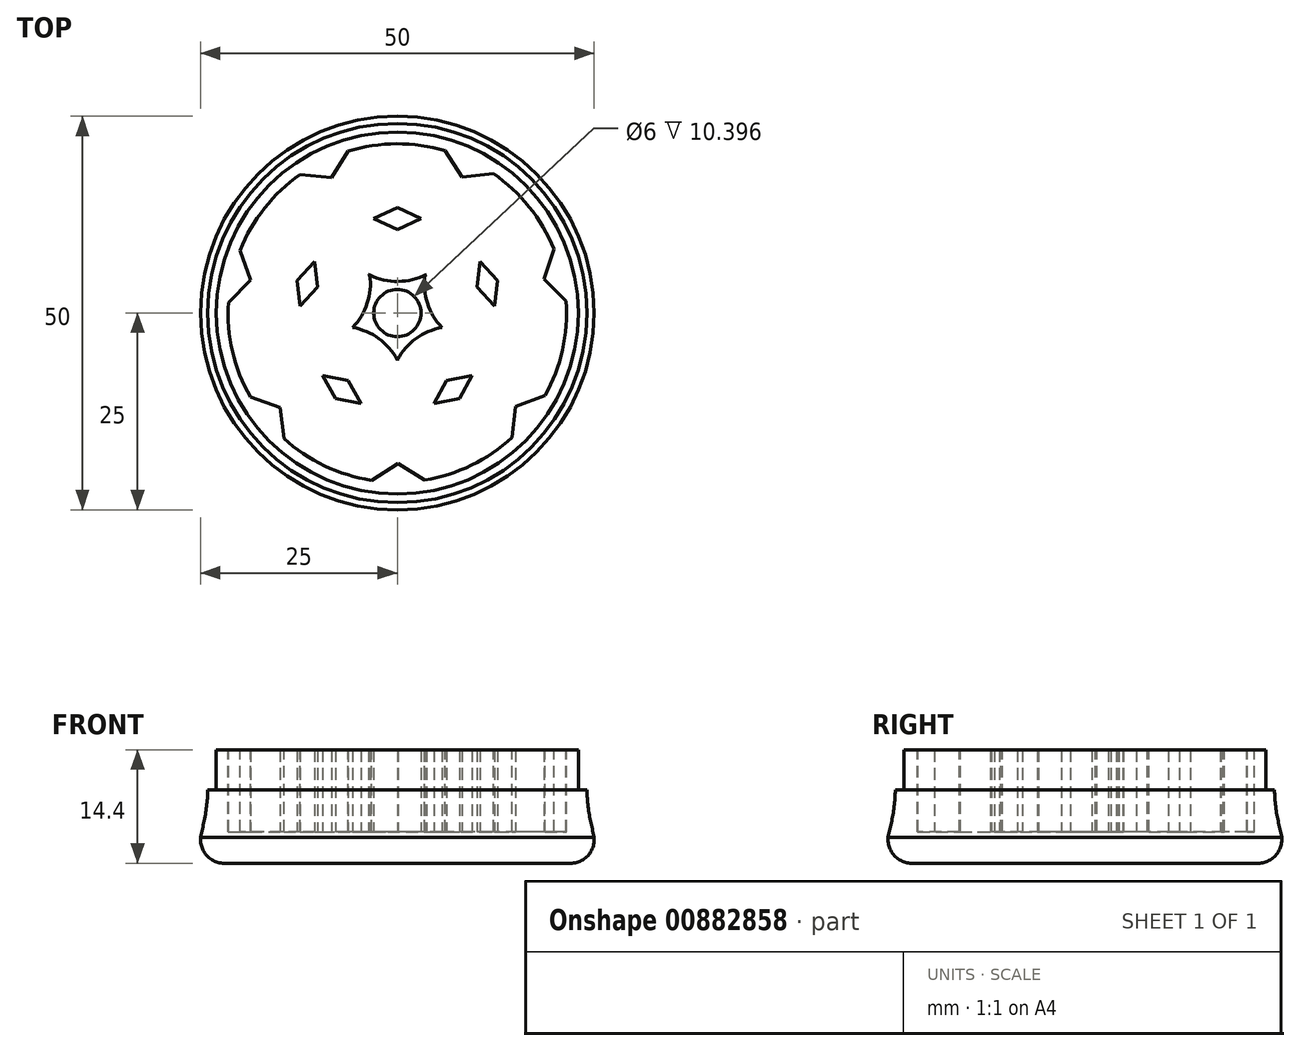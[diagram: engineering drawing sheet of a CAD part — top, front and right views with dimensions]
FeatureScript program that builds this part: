
annotation { "Feature Type Name" : "Feature", "Feature Type Description" : "" }
export const myFeature = defineFeature(function(context is Context, id is Id, definition is map)
    precondition{}
    {
        {
            var Q0;
            Q0=qCreatedBy(makeId("Top.planeOp"),FACE);
            var sketch = newSketch(context, id + "F0", { "sketchPlane" : qUnion([Q0])});
            skCircle(sketch, "E0", {"center": v(0, 0) * mm, "radius": 25 * mm});
            skSolve(sketch);
        }
        {
            var Q0;
            Q0=qSketchRegion(id+"F0",true);
            extrude(context, id + "F1", {"entities" : qUnion([Q0]), "depth" : 15 * mm, "offsetDistance" : 25 * mm});
        }
        {
            var Q0;
            Q0=makeQuery(id+"F1.opExtrude","CAP_EDGE",EDGE,{"disambiguationData":[OSD([sQuery(id+"F0.wireOp",EDGE,"E0")])],"isStart":true});
            fillet(context, id + "F2", {"entities" : qUnion([Q0]), "radius" : 3 * mm, "tangentPropagation" : true, "allowEdgeOverflow" : false});
        }
        {
            var Q0;
            Q0=qCreatedBy(makeId("Front.planeOp"),FACE);
            var sketch = newSketch(context, id + "F3", { "sketchPlane" : qUnion([Q0])});
            skLineSegment(sketch, "E1", {"start": v(0, 23.25) * mm, "end": v(0, 17.15) * mm});
            skLineSegment(sketch, "E2", {"start": v(0, 17.15) * mm, "end": v(0, 14.94) * mm});
            skLineSegment(sketch, "E3", {"start": v(0, 14.94) * mm, "end": v(25, 14.94) * mm});
            skFitSpline(sketch, "E4", {"points": [v(25, 14.94) * mm, v(24.1, 9.2) * mm, v(25, 3.32) * mm], "startDerivative": vector(-2.73, -11.51) * mm, "endDerivative": vector(2.72, -11.72) * mm});
            skLineSegment(sketch, "E5", {"start": v(25, 3.32) * mm, "end": v(27.42, 5.28) * mm});
            skLineSegment(sketch, "E6", {"start": v(27.42, 5.28) * mm, "end": v(25, 14.94) * mm});
            skSolve(sketch);
        }
        {
            var Q0;
            Q0=makeQuery(id+"F3.imprint","IMPRINT",FACE,{"disambiguationData":[TD([[makeQuery(id+"F3.imprint","IMPRINT",EDGE,{"derivedFrom":sQuery(id+"F3.wireOp",EDGE,"E4")}),1.0]])]});
            var Q1;
            Q1=sQuery(id+"F3.wireOp",EDGE,"E1");
            revolve(context, id + "F4", {"operationType" : NewBodyOperationType.REMOVE, "surfaceOperationType" : NewSurfaceOperationType.NEW, "entities" : qUnion([Q0]), "axis" : qUnion([Q1]), "revolveType" : RevolveType.FULL, "oppositeDirection" : true});
        }
        {
            var Q0;
            Q0=makeQuery(id+"F1.opExtrude","CAP_FACE",FACE,{"disambiguationData":[OSD([sQuery(id+"F0.wireOp",EDGE,"E0")])],"isStart":false});
            var sketch = newSketch(context, id + "F5", { "sketchPlane" : qUnion([Q0])});
            skCircle(sketch, "E7", {"center": v(0, 0) * mm, "radius": 21.5 * mm});
            skSolve(sketch);
        }
        {
            var Q0;
            Q0=qSketchRegion(id+"F5",true);
            extrude(context, id + "F6", {"entities" : qUnion([Q0]), "operationType" : NewBodyOperationType.REMOVE, "oppositeDirection" : true, "depth" : 11 * mm, "offsetDistance" : 25 * mm});
        }
        {
            var Q0;
            Q0=makeQuery(id+"F6.boolean.opBoolean","COPY",FACE,{"derivedFrom":makeQuery(id+"F6.opExtrude","CAP_FACE",FACE,{"disambiguationData":[OSD([sQuery(id+"F5.wireOp",EDGE,"E7")])],"isStart":false})});
            var sketch = newSketch(context, id + "F7", { "sketchPlane" : qUnion([Q0])});
            skCircle(sketch, "E8.cCircle", {"center": v(0, 0) * mm, "radius": 4.82 * mm, "construction": true});
            skLineSegment(sketch, "E8.0", {"start": v(-3.5, 4.82) * mm, "end": v(-3.5, 4.82) * mm});
            skLineSegment(sketch, "E8.1", {"start": v(3.5, 4.82) * mm, "end": v(3.5, 4.81) * mm});
            skLineSegment(sketch, "E8.2", {"start": v(5.66, -1.84) * mm, "end": v(5.66, -1.84) * mm});
            skLineSegment(sketch, "E8.3", {"start": v(0, -5.95) * mm, "end": v(-2.83, -3.9) * mm});
            skLineSegment(sketch, "E8.4", {"start": v(-5.66, -1.84) * mm, "end": v(-5.66, -1.83) * mm});
            skPoint(sketch, "E8.0.midPoint", {"position": v(0, 4.82) * mm});
            skCircle(sketch, "E9", {"center": v(0, 0) * mm, "radius": 3 * mm});
            skLineSegment(sketch, "E10", {"start": v(-3.69, 4.91) * mm, "end": v(-3.5, 4.82) * mm});
            skLineSegment(sketch, "E11", {"start": v(3.5, 4.82) * mm, "end": v(3.69, 4.91) * mm});
            skPoint(sketch, "E12.visualSharp", {"position": v(0, 3) * mm});
            skArc(sketch, "E12.filletArc", {"start": v(-3.69, 4.91) * mm, "mid": v(0, 4.01) * mm, "end": v(3.69, 4.91) * mm});
            skArc(sketch, "E13.1.0", {"start": v(-5.81, -1.99) * mm, "mid": v(-3.82, 1.24) * mm, "end": v(-3.53, 5.02) * mm});
            skArc(sketch, "E13.2.0", {"start": v(0.1, -6.14) * mm, "mid": v(-2.36, -3.25) * mm, "end": v(-5.87, -1.8) * mm});
            skArc(sketch, "E13.3.0", {"start": v(5.87, -1.8) * mm, "mid": v(2.36, -3.25) * mm, "end": v(-0.1, -6.14) * mm});
            skArc(sketch, "E13.4.0", {"start": v(3.53, 5.02) * mm, "mid": v(3.82, 1.24) * mm, "end": v(5.81, -1.99) * mm});
            skLineSegment(sketch, "E14.trimOffspring", {"start": v(4.58, 1.49) * mm, "end": v(5.66, -1.84) * mm});
            skLineSegment(sketch, "E15.trimOffspring", {"start": v(2.83, -3.9) * mm, "end": v(0, -5.95) * mm});
            skLineSegment(sketch, "E16.trimOffspring", {"start": v(-5.66, -1.84) * mm, "end": v(-5.66, -1.84) * mm});
            skLineSegment(sketch, "E17.trimOffspring", {"start": v(-4.58, 1.49) * mm, "end": v(-3.5, 4.82) * mm});
            skLineSegment(sketch, "E18", {"start": v(0, 0) * mm, "end": v(0, 12.01) * mm});
            skLineSegment(sketch, "E19", {"start": v(0, 12.01) * mm, "end": v(3, 12.01) * mm});
            skLineSegment(sketch, "E20", {"start": v(3, 12.01) * mm, "end": v(0, 10.64) * mm});
            skLineSegment(sketch, "E21.MirrorCS", {"start": v(3, 12.01) * mm, "end": v(0, 13.4) * mm});
            skLineSegment(sketch, "E22.MirrorCS", {"start": v(-3, 12.01) * mm, "end": v(0, 10.64) * mm});
            skLineSegment(sketch, "E23.MirrorCS", {"start": v(-3, 12.01) * mm, "end": v(0, 13.4) * mm});
            skLineSegment(sketch, "E24.1.0", {"start": v(-12.35, 0.86) * mm, "end": v(-10.12, 3.29) * mm});
            skLineSegment(sketch, "E24.1.1", {"start": v(-10.5, 6.57) * mm, "end": v(-10.12, 3.29) * mm});
            skLineSegment(sketch, "E24.1.2", {"start": v(-10.5, 6.57) * mm, "end": v(-12.74, 4.14) * mm});
            skLineSegment(sketch, "E24.1.3", {"start": v(-12.35, 0.86) * mm, "end": v(-12.74, 4.14) * mm});
            skLineSegment(sketch, "E24.2.0", {"start": v(-4.63, -11.48) * mm, "end": v(-6.25, -8.6) * mm});
            skLineSegment(sketch, "E24.2.1", {"start": v(-9.49, -7.96) * mm, "end": v(-6.25, -8.6) * mm});
            skLineSegment(sketch, "E24.2.2", {"start": v(-9.49, -7.96) * mm, "end": v(-7.87, -10.83) * mm});
            skLineSegment(sketch, "E24.2.3", {"start": v(-4.63, -11.48) * mm, "end": v(-7.87, -10.83) * mm});
            skLineSegment(sketch, "E24.3.0", {"start": v(9.49, -7.96) * mm, "end": v(6.25, -8.6) * mm});
            skLineSegment(sketch, "E24.3.1", {"start": v(4.63, -11.48) * mm, "end": v(6.25, -8.6) * mm});
            skLineSegment(sketch, "E24.3.2", {"start": v(4.63, -11.48) * mm, "end": v(7.87, -10.83) * mm});
            skLineSegment(sketch, "E24.3.3", {"start": v(9.49, -7.96) * mm, "end": v(7.87, -10.83) * mm});
            skLineSegment(sketch, "E24.4.0", {"start": v(10.5, 6.57) * mm, "end": v(10.12, 3.29) * mm});
            skLineSegment(sketch, "E24.4.1", {"start": v(12.35, 0.86) * mm, "end": v(10.12, 3.29) * mm});
            skLineSegment(sketch, "E24.4.2", {"start": v(12.35, 0.86) * mm, "end": v(12.74, 4.14) * mm});
            skLineSegment(sketch, "E24.4.3", {"start": v(10.5, 6.57) * mm, "end": v(12.74, 4.14) * mm});
            skLineSegment(sketch, "E25", {"start": v(0, 0) * mm, "end": v(0.1, -21.5) * mm});
            skLineSegment(sketch, "E26", {"start": v(0.1, -21.5) * mm, "end": v(3.92, -21.48) * mm});
            skLineSegment(sketch, "E27", {"start": v(3.92, -21.48) * mm, "end": v(0.08, -19.13) * mm});
            skLineSegment(sketch, "E28.MirrorCS", {"start": v(-3.73, -21.52) * mm, "end": v(0.08, -19.13) * mm});
            skLineSegment(sketch, "E29.MirrorCS", {"start": v(0.1, -21.5) * mm, "end": v(-3.73, -21.52) * mm});
            skLineSegment(sketch, "E30.1.0", {"start": v(19.24, -10.33) * mm, "end": v(15, -11.86) * mm});
            skLineSegment(sketch, "E30.1.1", {"start": v(14.5, -16.33) * mm, "end": v(15, -11.86) * mm});
            skLineSegment(sketch, "E30.1.2", {"start": v(16.87, -13.33) * mm, "end": v(19.24, -10.33) * mm});
            skLineSegment(sketch, "E30.1.3", {"start": v(16.87, -13.33) * mm, "end": v(14.5, -16.33) * mm});
            skLineSegment(sketch, "E30.2.0", {"start": v(20.07, 8.6) * mm, "end": v(18.63, 4.34) * mm});
            skLineSegment(sketch, "E30.2.1", {"start": v(21.8, 1.15) * mm, "end": v(18.63, 4.34) * mm});
            skLineSegment(sketch, "E30.2.2", {"start": v(20.94, 4.88) * mm, "end": v(20.07, 8.6) * mm});
            skLineSegment(sketch, "E30.2.3", {"start": v(20.94, 4.88) * mm, "end": v(21.8, 1.15) * mm});
            skLineSegment(sketch, "E30.3.0", {"start": v(5.8, 21.06) * mm, "end": v(8.22, 17.27) * mm});
            skLineSegment(sketch, "E30.3.1", {"start": v(12.7, 17.77) * mm, "end": v(8.22, 17.27) * mm});
            skLineSegment(sketch, "E30.3.2", {"start": v(9.24, 19.41) * mm, "end": v(5.8, 21.06) * mm});
            skLineSegment(sketch, "E30.3.3", {"start": v(9.24, 19.41) * mm, "end": v(12.7, 17.77) * mm});
            skLineSegment(sketch, "E30.4.0", {"start": v(-12.85, 17.66) * mm, "end": v(-8.37, 17.2) * mm});
            skLineSegment(sketch, "E30.4.1", {"start": v(-5.98, 21) * mm, "end": v(-8.37, 17.2) * mm});
            skLineSegment(sketch, "E30.4.2", {"start": v(-9.41, 19.33) * mm, "end": v(-12.85, 17.66) * mm});
            skLineSegment(sketch, "E30.4.3", {"start": v(-9.41, 19.33) * mm, "end": v(-5.98, 21) * mm});
            skLineSegment(sketch, "E30.5.0", {"start": v(-21.82, 0.96) * mm, "end": v(-18.67, 4.17) * mm});
            skLineSegment(sketch, "E30.5.1", {"start": v(-20.15, 8.42) * mm, "end": v(-18.67, 4.17) * mm});
            skLineSegment(sketch, "E30.5.2", {"start": v(-20.98, 4.7) * mm, "end": v(-21.82, 0.96) * mm});
            skLineSegment(sketch, "E30.5.3", {"start": v(-20.98, 4.7) * mm, "end": v(-20.15, 8.42) * mm});
            skLineSegment(sketch, "E30.6.0", {"start": v(-14.35, -16.46) * mm, "end": v(-14.9, -12) * mm});
            skLineSegment(sketch, "E30.6.1", {"start": v(-19.15, -10.5) * mm, "end": v(-14.9, -12) * mm});
            skLineSegment(sketch, "E30.6.2", {"start": v(-16.75, -13.48) * mm, "end": v(-14.35, -16.46) * mm});
            skLineSegment(sketch, "E30.6.3", {"start": v(-16.75, -13.48) * mm, "end": v(-19.15, -10.5) * mm});
            skSolve(sketch);
        }
        {
            var Q0;
            Q0=qSketchRegion(id+"F7",true);
            extrude(context, id + "F8", {"entities" : qUnion([Q0]), "operationType" : NewBodyOperationType.ADD, "depth" : 10.8 * mm, "offsetDistance" : 25 * mm});
        }
        {
            var Q0;
            Q0=makeQuery(id+"F1.opExtrude","CAP_FACE",FACE,{"disambiguationData":[OSD([sQuery(id+"F0.wireOp",EDGE,"E0")])],"isStart":false});
            var sketch = newSketch(context, id + "F9", { "sketchPlane" : qUnion([Q0])});
            skCircle(sketch, "E31", {"center": v(0, 0) * mm, "radius": 23 * mm});
            skCircle(sketch, "E32", {"center": v(0, 0) * mm, "radius": 26.27 * mm});
            skSolve(sketch);
        }
        {
            var Q0;
            Q0 = qSketchRegion(id + "F9", true);
            extrude(context, id + "F10", {"entities" : qUnion([Q0]), "operationType" : NewBodyOperationType.REMOVE, "oppositeDirection" : true, "depth" : 5.7 * mm, "offsetDistance" : 25 * mm});
        }
        {
            var Q0;
            Q0=qCreatedBy(makeId("Right.planeOp"),FACE);
            var sketch = newSketch(context, id + "F11", { "sketchPlane" : qUnion([Q0])});
            skLineSegment(sketch, "E33.bottom", {"start": v(-34.02, 32) * mm, "end": v(28.83, 32) * mm});
            skLineSegment(sketch, "E33.top", {"start": v(-34.02, 14.4) * mm, "end": v(28.83, 14.4) * mm});
            skLineSegment(sketch, "E33.left", {"start": v(-34.02, 32) * mm, "end": v(-34.02, 14.4) * mm});
            skLineSegment(sketch, "E33.right", {"start": v(28.83, 32) * mm, "end": v(28.83, 14.4) * mm});
            skSolve(sketch);
        }
        {
            var Q0;
            Q0 = qSketchRegion(id + "F11", true);
            extrude(context, id + "F12", {"entities" : qUnion([Q0]), "operationType" : NewBodyOperationType.REMOVE, "endBound" : BoundingType.SYMMETRIC, "depth" : 60 * mm, "offsetDistance" : 25 * mm});
        }
    });
